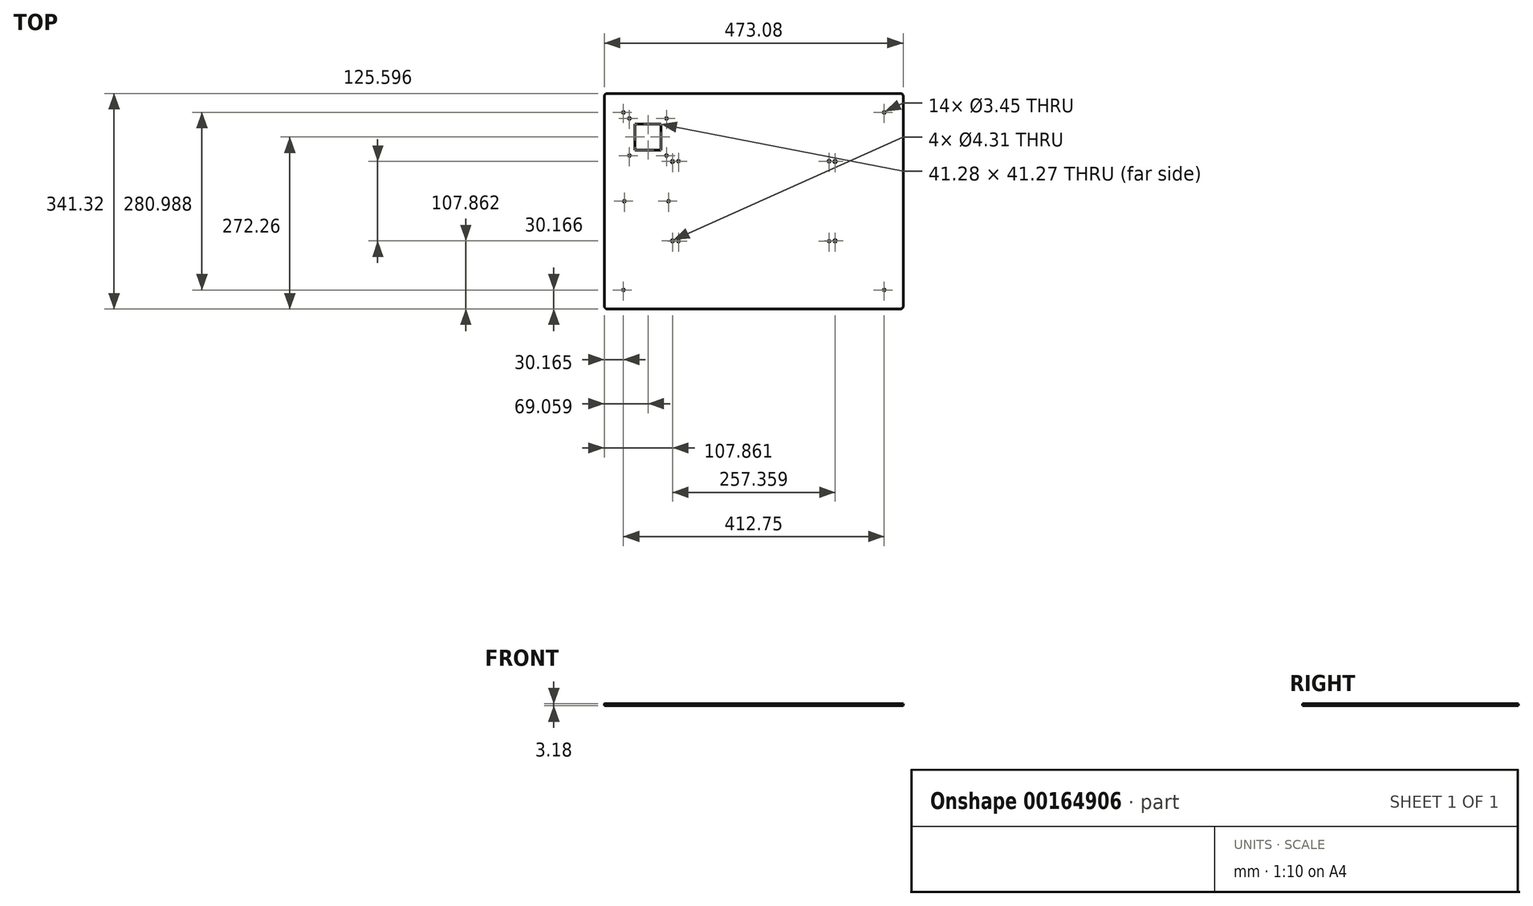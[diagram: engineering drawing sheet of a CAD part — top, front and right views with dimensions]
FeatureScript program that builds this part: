
annotation { "Feature Type Name" : "Feature", "Feature Type Description" : "" }
export const myFeature = defineFeature(function(context is Context, id is Id, definition is map)
    precondition{}
    {
        {
            var Q0;
            Q0=qCreatedBy(makeId("Top.planeOp"),FACE);
            var sketch = newSketch(context, id + "F0", { "sketchPlane" : qUnion([Q0])});
            skLineSegment(sketch, "E0.bottom", {"start": v(236.54, 170.66) * mm, "end": v(-236.54, 170.66) * mm});
            skLineSegment(sketch, "E0.top", {"start": v(236.54, -170.66) * mm, "end": v(-236.54, -170.66) * mm});
            skLineSegment(sketch, "E0.left", {"start": v(236.54, 170.66) * mm, "end": v(236.54, -170.66) * mm});
            skLineSegment(sketch, "E0.right", {"start": v(-236.54, 170.66) * mm, "end": v(-236.54, -170.66) * mm});
            skPoint(sketch, "E0.middle", {"position": v(0, 0) * mm});
            skLineSegment(sketch, "E1", {"start": v(0, 101.6) * mm, "end": v(0, 0) * mm, "construction": true});
            skLineSegment(sketch, "E2", {"start": v(0, 101.6) * mm, "end": v(-167.48, 101.6) * mm, "construction": true});
            skLineSegment(sketch, "E3.bottom", {"start": v(-138.11, 72.23) * mm, "end": v(-196.85, 72.23) * mm, "construction": true});
            skLineSegment(sketch, "E3.top", {"start": v(-138.11, 130.97) * mm, "end": v(-196.85, 130.97) * mm, "construction": true});
            skLineSegment(sketch, "E3.left", {"start": v(-138.11, 72.23) * mm, "end": v(-138.11, 130.97) * mm, "construction": true});
            skLineSegment(sketch, "E3.right", {"start": v(-196.85, 72.23) * mm, "end": v(-196.85, 130.97) * mm, "construction": true});
            skPoint(sketch, "E3.middle", {"position": v(-167.48, 101.6) * mm});
            skCircle(sketch, "E4", {"center": v(-196.85, 130.97) * mm, "radius": 1.73 * mm});
            skCircle(sketch, "E5", {"center": v(-138.11, 130.97) * mm, "radius": 1.73 * mm});
            skCircle(sketch, "E6", {"center": v(-138.11, 72.23) * mm, "radius": 1.73 * mm});
            skCircle(sketch, "E7", {"center": v(-196.85, 72.23) * mm, "radius": 1.73 * mm});
            skLineSegment(sketch, "E8", {"start": v(0, 0) * mm, "end": v(-119.17, 63.3) * mm, "construction": true});
            skLineSegment(sketch, "E9", {"start": v(0, 0) * mm, "end": v(-119.17, 0) * mm, "construction": true});
            skLineSegment(sketch, "E10", {"start": v(0, 0) * mm, "end": v(119.17, 0) * mm, "construction": true});
            skLineSegment(sketch, "E11", {"start": v(0, 0) * mm, "end": v(-119.17, -63.3) * mm, "construction": true});
            skLineSegment(sketch, "E12", {"start": v(0, 0) * mm, "end": v(119.17, -63.3) * mm, "construction": true});
            skLineSegment(sketch, "E13", {"start": v(0, 0) * mm, "end": v(119.17, 63.3) * mm, "construction": true});
            skLineSegment(sketch, "E14", {"start": v(119.17, -63.3) * mm, "end": v(119.17, 63.3) * mm, "construction": true});
            skLineSegment(sketch, "E15", {"start": v(-119.17, -63.3) * mm, "end": v(-119.17, 63.3) * mm, "construction": true});
            skCircle(sketch, "E16", {"center": v(-119.17, -63.3) * mm, "radius": 1.73 * mm});
            skCircle(sketch, "E17", {"center": v(-119.17, 63.3) * mm, "radius": 1.73 * mm});
            skCircle(sketch, "E18", {"center": v(119.17, -63.3) * mm, "radius": 1.73 * mm});
            skCircle(sketch, "E19", {"center": v(119.17, 63.3) * mm, "radius": 1.73 * mm});
            skLineSegment(sketch, "E20.bottom", {"start": v(-128.68, 62.8) * mm, "end": v(128.68, 62.8) * mm, "construction": true});
            skLineSegment(sketch, "E20.top", {"start": v(-128.68, -62.8) * mm, "end": v(128.68, -62.8) * mm, "construction": true});
            skLineSegment(sketch, "E20.left", {"start": v(-128.68, 62.8) * mm, "end": v(-128.68, -62.8) * mm, "construction": true});
            skLineSegment(sketch, "E20.right", {"start": v(128.68, 62.8) * mm, "end": v(128.68, -62.8) * mm, "construction": true});
            skCircle(sketch, "E21", {"center": v(-128.68, -62.8) * mm, "radius": 2.15 * mm});
            skCircle(sketch, "E22", {"center": v(-128.68, 62.8) * mm, "radius": 2.15 * mm});
            skCircle(sketch, "E23", {"center": v(128.68, -62.8) * mm, "radius": 2.15 * mm});
            skCircle(sketch, "E24", {"center": v(128.68, 62.8) * mm, "radius": 2.15 * mm});
            skLineSegment(sketch, "E25", {"start": v(128.68, -62.8) * mm, "end": v(236.54, -62.8) * mm, "construction": true});
            skLineSegment(sketch, "E26", {"start": v(128.68, -62.8) * mm, "end": v(128.68, -170.66) * mm, "construction": true});
            skCircle(sketch, "E27", {"center": v(-119.17, -63.3) * mm, "radius": 4.76 * mm, "construction": true});
            skCircle(sketch, "E28", {"center": v(-128.68, -62.8) * mm, "radius": 4.76 * mm, "construction": true});
            skLineSegment(sketch, "E29.bottom", {"start": v(-188.12, 122.24) * mm, "end": v(-146.84, 122.24) * mm});
            skLineSegment(sketch, "E29.top", {"start": v(-188.12, 80.96) * mm, "end": v(-146.84, 80.96) * mm});
            skLineSegment(sketch, "E29.left", {"start": v(-188.12, 122.24) * mm, "end": v(-188.12, 80.96) * mm});
            skLineSegment(sketch, "E29.right", {"start": v(-146.84, 122.24) * mm, "end": v(-146.84, 80.96) * mm});
            skLineSegment(sketch, "E30.bottom", {"start": v(-206.38, 140.5) * mm, "end": v(206.38, 140.5) * mm, "construction": true});
            skLineSegment(sketch, "E30.top", {"start": v(-206.38, -140.5) * mm, "end": v(206.38, -140.5) * mm, "construction": true});
            skLineSegment(sketch, "E30.left", {"start": v(-206.38, 140.5) * mm, "end": v(-206.38, -140.5) * mm, "construction": true});
            skLineSegment(sketch, "E30.right", {"start": v(206.38, 140.5) * mm, "end": v(206.38, -140.5) * mm, "construction": true});
            skLineSegment(sketch, "E31", {"start": v(-196.85, 130.97) * mm, "end": v(-206.38, 130.97) * mm, "construction": true});
            skLineSegment(sketch, "E32", {"start": v(-196.85, 130.97) * mm, "end": v(-196.85, 140.5) * mm, "construction": true});
            skLineSegment(sketch, "E33", {"start": v(-206.38, 140.5) * mm, "end": v(-236.54, 140.5) * mm, "construction": true});
            skSolve(sketch);
        }
        {
            var Q0;
            Q0 = qSketchRegion(id + "F0", true);
            extrude(context, id + "F1", {"entities" : qUnion([Q0]), "depth" : 3.17 * mm});
        }
        {
            var Q0;
            Q0=makeQuery(id+"F1.opExtrude","CAP_FACE",FACE,{"disambiguationData":[OSD([sQuery(id+"F0.wireOp",EDGE,"E0.bottom"),sQuery(id+"F0.wireOp",EDGE,"E0.top"),sQuery(id+"F0.wireOp",EDGE,"E0.left"),sQuery(id+"F0.wireOp",EDGE,"E0.right"),sQuery(id+"F0.wireOp",EDGE,"E4"),sQuery(id+"F0.wireOp",EDGE,"E5"),sQuery(id+"F0.wireOp",EDGE,"E6"),sQuery(id+"F0.wireOp",EDGE,"E7"),sQuery(id+"F0.wireOp",EDGE,"E16"),sQuery(id+"F0.wireOp",EDGE,"E17"),sQuery(id+"F0.wireOp",EDGE,"E18"),sQuery(id+"F0.wireOp",EDGE,"E19"),sQuery(id+"F0.wireOp",EDGE,"E21"),sQuery(id+"F0.wireOp",EDGE,"E22"),sQuery(id+"F0.wireOp",EDGE,"E23"),sQuery(id+"F0.wireOp",EDGE,"E24")])],"isStart":false});
            var sketch = newSketch(context, id + "F2", { "sketchPlane" : qUnion([Q0])});
            skLineSegment(sketch, "E34.bottom", {"start": v(-206.38, 140.5) * mm, "end": v(206.38, 140.5) * mm, "construction": true});
            skLineSegment(sketch, "E34.top", {"start": v(-206.38, -140.5) * mm, "end": v(206.38, -140.5) * mm, "construction": true});
            skLineSegment(sketch, "E34.left", {"start": v(-206.38, 140.5) * mm, "end": v(-206.38, -140.5) * mm, "construction": true});
            skLineSegment(sketch, "E34.right", {"start": v(206.38, 140.5) * mm, "end": v(206.38, -140.5) * mm, "construction": true});
            skPoint(sketch, "E34.middle", {"position": v(0, 0) * mm});
            skLineSegment(sketch, "E35.bottom", {"start": v(-206.38, 140.5) * mm, "end": v(-236.54, 140.5) * mm, "construction": true});
            skLineSegment(sketch, "E35.top", {"start": v(-206.38, 170.66) * mm, "end": v(-236.54, 170.66) * mm, "construction": true});
            skLineSegment(sketch, "E35.left", {"start": v(-206.38, 140.5) * mm, "end": v(-206.38, 170.66) * mm, "construction": true});
            skLineSegment(sketch, "E35.right", {"start": v(-236.54, 140.5) * mm, "end": v(-236.54, 170.66) * mm, "construction": true});
            skCircle(sketch, "E36", {"center": v(-206.38, -140.5) * mm, "radius": 1.73 * mm});
            skCircle(sketch, "E37", {"center": v(-206.38, 140.5) * mm, "radius": 1.73 * mm});
            skCircle(sketch, "E38", {"center": v(206.38, 140.5) * mm, "radius": 1.73 * mm});
            skCircle(sketch, "E39", {"center": v(206.38, -140.5) * mm, "radius": 1.73 * mm});
            skLineSegment(sketch, "E40", {"start": v(-196.85, 72.23) * mm, "end": v(-206.38, 72.23) * mm, "construction": true});
            skLineSegment(sketch, "E41", {"start": v(-196.85, 72.23) * mm, "end": v(-196.85, -140.5) * mm, "construction": true});
            skSolve(sketch);
        }
        {
            var Q0;
            Q0=makeQuery(id+"F1.opExtrude","SWEPT_EDGE",EDGE,{"disambiguationData":[OSD([sQuery(id+"F0.wireOp",EDGE,"E0.top"),sQuery(id+"F0.wireOp",EDGE,"E0.left")])]});
            var Q1;
            Q1=makeQuery(id+"F1.opExtrude","SWEPT_EDGE",EDGE,{"disambiguationData":[OSD([sQuery(id+"F0.wireOp",EDGE,"E0.bottom"),sQuery(id+"F0.wireOp",EDGE,"E0.left")])]});
            var Q2;
            Q2=makeQuery(id+"F1.opExtrude","SWEPT_EDGE",EDGE,{"disambiguationData":[OSD([sQuery(id+"F0.wireOp",EDGE,"E0.bottom"),sQuery(id+"F0.wireOp",EDGE,"E0.right")])]});
            var Q3;
            Q3=makeQuery(id+"F1.opExtrude","SWEPT_EDGE",EDGE,{"disambiguationData":[OSD([sQuery(id+"F0.wireOp",EDGE,"E0.top"),sQuery(id+"F0.wireOp",EDGE,"E0.right")])]});
            fillet(context, id + "F3", {"entities" : qUnion([Q0, Q1, Q2, Q3]), "radius" : 4.76 * mm, "tangentPropagation" : true, "allowEdgeOverflow" : false});
        }
        {
            var Q0;
            Q0 = qSketchRegion(id + "F2", true);
            var Q1;
            Q1=makeQuery(id+"F1.opExtrude","CAP_FACE",FACE,{"disambiguationData":[OSD([sQuery(id+"F0.wireOp",EDGE,"E0.bottom"),sQuery(id+"F0.wireOp",EDGE,"E0.top"),sQuery(id+"F0.wireOp",EDGE,"E0.left"),sQuery(id+"F0.wireOp",EDGE,"E0.right"),sQuery(id+"F0.wireOp",EDGE,"E4"),sQuery(id+"F0.wireOp",EDGE,"E5"),sQuery(id+"F0.wireOp",EDGE,"E6"),sQuery(id+"F0.wireOp",EDGE,"E7"),sQuery(id+"F0.wireOp",EDGE,"E16"),sQuery(id+"F0.wireOp",EDGE,"E17"),sQuery(id+"F0.wireOp",EDGE,"E18"),sQuery(id+"F0.wireOp",EDGE,"E19"),sQuery(id+"F0.wireOp",EDGE,"E21"),sQuery(id+"F0.wireOp",EDGE,"E22"),sQuery(id+"F0.wireOp",EDGE,"E23"),sQuery(id+"F0.wireOp",EDGE,"E24")])],"isStart":true});
            extrude(context, id + "F4", {"entities" : qUnion([Q0]), "operationType" : NewBodyOperationType.REMOVE, "endBound" : BoundingType.UP_TO_SURFACE, "oppositeDirection" : true, "endBoundEntityFace" : qUnion([Q1]), "depth" : 25.4 * mm});
        }
        {
            var Q0;
            Q0=makeQuery(id+"F1.opExtrude","CAP_FACE",FACE,{"disambiguationData":[OSD([sQuery(id+"F0.wireOp",EDGE,"E0.bottom"),sQuery(id+"F0.wireOp",EDGE,"E0.top"),sQuery(id+"F0.wireOp",EDGE,"E0.left"),sQuery(id+"F0.wireOp",EDGE,"E0.right"),sQuery(id+"F0.wireOp",EDGE,"E4"),sQuery(id+"F0.wireOp",EDGE,"E5"),sQuery(id+"F0.wireOp",EDGE,"E6"),sQuery(id+"F0.wireOp",EDGE,"E7"),sQuery(id+"F0.wireOp",EDGE,"E16"),sQuery(id+"F0.wireOp",EDGE,"E17"),sQuery(id+"F0.wireOp",EDGE,"E18"),sQuery(id+"F0.wireOp",EDGE,"E19"),sQuery(id+"F0.wireOp",EDGE,"E21"),sQuery(id+"F0.wireOp",EDGE,"E22"),sQuery(id+"F0.wireOp",EDGE,"E23"),sQuery(id+"F0.wireOp",EDGE,"E24"),sQuery(id+"F0.wireOp",EDGE,"E29.bottom"),sQuery(id+"F0.wireOp",EDGE,"E29.top"),sQuery(id+"F0.wireOp",EDGE,"E29.left"),sQuery(id+"F0.wireOp",EDGE,"E29.right")])],"isStart":false});
            var sketch = newSketch(context, id + "F5", { "sketchPlane" : qUnion([Q0])});
            skLineSegment(sketch, "E42", {"start": v(-236.54, 0) * mm, "end": v(-204.79, 0) * mm, "construction": true});
            skLineSegment(sketch, "E43", {"start": v(-204.79, 0) * mm, "end": v(-134.94, 0) * mm, "construction": true});
            skLineSegment(sketch, "E44", {"start": v(-119.17, 63.3) * mm, "end": v(-119.17, -63.3) * mm, "construction": true});
            skLineSegment(sketch, "E45", {"start": v(-119.17, 0) * mm, "end": v(-134.94, 0) * mm, "construction": true});
            skCircle(sketch, "E46", {"center": v(-134.94, 0) * mm, "radius": 1.73 * mm});
            skCircle(sketch, "E47", {"center": v(-204.79, 0) * mm, "radius": 1.73 * mm});
            skSolve(sketch);
        }
        {
            var Q0;
            Q0 = qSketchRegion(id + "F5", true);
            var Q1;
            Q1=makeQuery(id+"F1.opExtrude","CAP_FACE",FACE,{"disambiguationData":[OSD([sQuery(id+"F0.wireOp",EDGE,"E0.bottom"),sQuery(id+"F0.wireOp",EDGE,"E0.top"),sQuery(id+"F0.wireOp",EDGE,"E0.left"),sQuery(id+"F0.wireOp",EDGE,"E0.right"),sQuery(id+"F0.wireOp",EDGE,"E4"),sQuery(id+"F0.wireOp",EDGE,"E5"),sQuery(id+"F0.wireOp",EDGE,"E6"),sQuery(id+"F0.wireOp",EDGE,"E7"),sQuery(id+"F0.wireOp",EDGE,"E16"),sQuery(id+"F0.wireOp",EDGE,"E17"),sQuery(id+"F0.wireOp",EDGE,"E18"),sQuery(id+"F0.wireOp",EDGE,"E19"),sQuery(id+"F0.wireOp",EDGE,"E21"),sQuery(id+"F0.wireOp",EDGE,"E22"),sQuery(id+"F0.wireOp",EDGE,"E23"),sQuery(id+"F0.wireOp",EDGE,"E24"),sQuery(id+"F0.wireOp",EDGE,"E29.bottom"),sQuery(id+"F0.wireOp",EDGE,"E29.top"),sQuery(id+"F0.wireOp",EDGE,"E29.left"),sQuery(id+"F0.wireOp",EDGE,"E29.right")])],"isStart":true});
            extrude(context, id + "F6", {"entities" : qUnion([Q0]), "operationType" : NewBodyOperationType.REMOVE, "endBound" : BoundingType.UP_TO_SURFACE, "oppositeDirection" : true, "endBoundEntityFace" : qUnion([Q1]), "depth" : 25.4 * mm});
        }
    });
